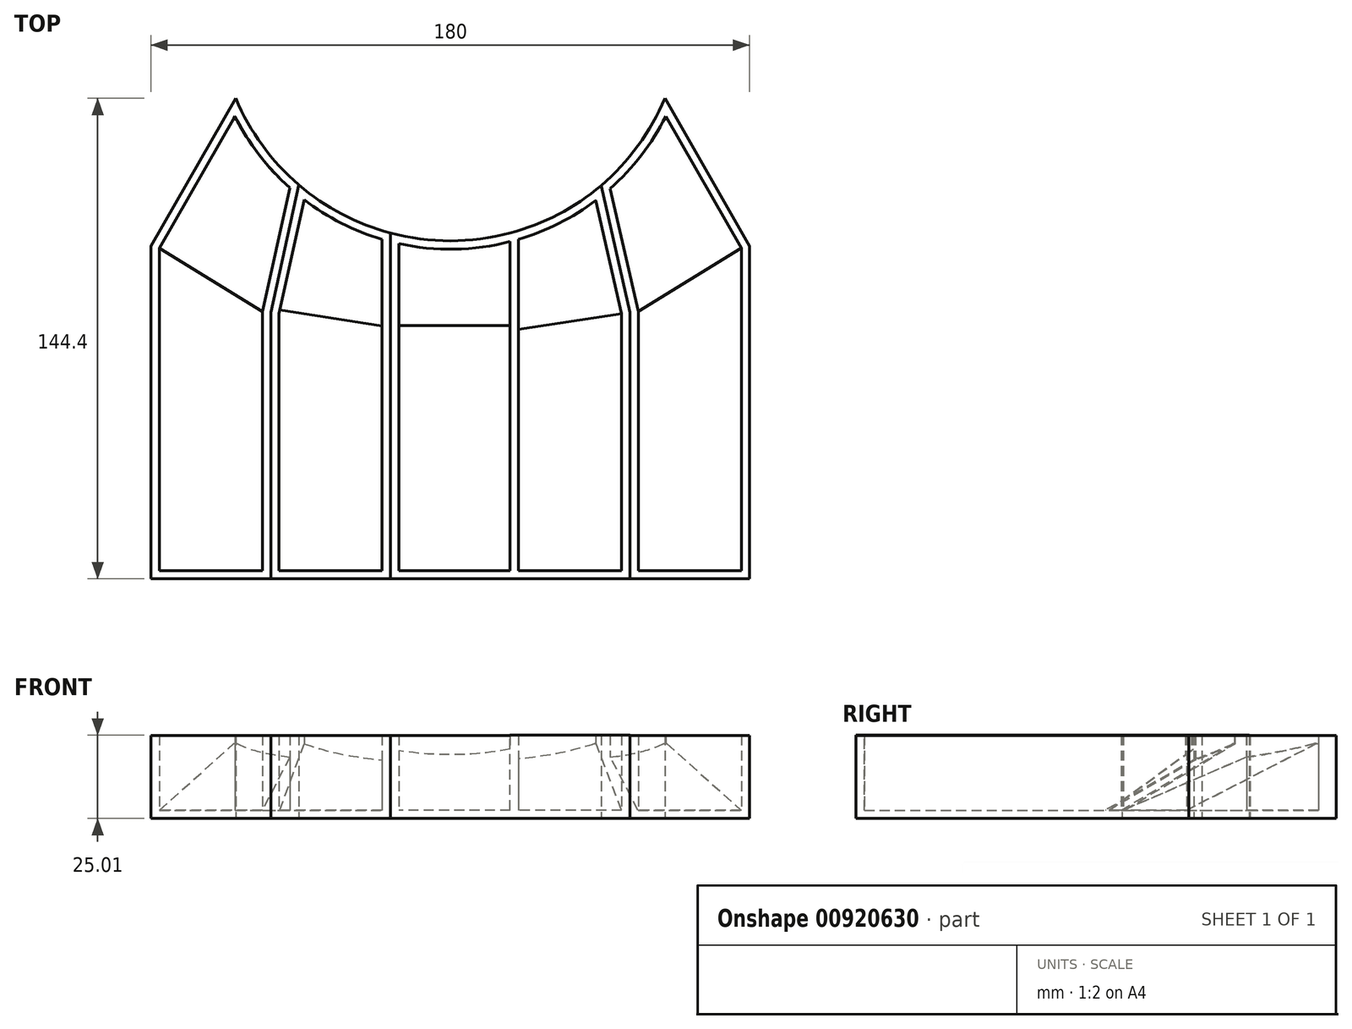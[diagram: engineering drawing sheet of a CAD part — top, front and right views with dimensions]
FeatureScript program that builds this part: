
annotation { "Feature Type Name" : "Feature", "Feature Type Description" : "" }
export const myFeature = defineFeature(function(context is Context, id is Id, definition is map)
    precondition{}
    {
        {
            var Q0;
            Q0=qCreatedBy(makeId("Top.planeOp"),FACE);
            var sketch = newSketch(context, id + "F0", { "sketchPlane" : qUnion([Q0])});
            skLineSegment(sketch, "E0", {"start": v(-90, -21.59) * mm, "end": v(90, -21.59) * mm});
            skLineSegment(sketch, "E1", {"start": v(-90, -21.59) * mm, "end": v(-90, 28.41) * mm});
            skLineSegment(sketch, "E2", {"start": v(90, 28.41) * mm, "end": v(90, -21.59) * mm});
            skLineSegment(sketch, "E3", {"start": v(-90, 28.41) * mm, "end": v(-90, 78.41) * mm});
            skLineSegment(sketch, "E4", {"start": v(-90, 78.41) * mm, "end": v(-64.5, 122.8) * mm});
            skLineSegment(sketch, "E5", {"start": v(90, 28.41) * mm, "end": v(90, 78.41) * mm});
            skLineSegment(sketch, "E6", {"start": v(90, 78.41) * mm, "end": v(64.5, 122.8) * mm});
            skLineSegment(sketch, "E7", {"start": v(-54, -21.59) * mm, "end": v(-54, 28.41) * mm});
            skLineSegment(sketch, "E8", {"start": v(-18, 28.41) * mm, "end": v(-18, -21.59) * mm});
            skLineSegment(sketch, "E9", {"start": v(54, 28.41) * mm, "end": v(54, -21.59) * mm});
            skLineSegment(sketch, "E10", {"start": v(18, 28.41) * mm, "end": v(18, -21.59) * mm});
            skArc(sketch, "E11", {"start": v(-64.5, 122.8) * mm, "mid": v(0, 79.98) * mm, "end": v(64.5, 122.8) * mm});
            skArc(sketch, "E12", {"start": v(-64.5, 122.8) * mm, "mid": v(0, 80.25) * mm, "end": v(64.5, 122.8) * mm});
            skLineSegment(sketch, "E13", {"start": v(-54, 28.41) * mm, "end": v(-54, 58.41) * mm});
            skLineSegment(sketch, "E14", {"start": v(-18, 28.41) * mm, "end": v(-18, 82.33) * mm});
            skLineSegment(sketch, "E15", {"start": v(18, 28.41) * mm, "end": v(18, 82.33) * mm});
            skLineSegment(sketch, "E16", {"start": v(54, 28.41) * mm, "end": v(54, 58.41) * mm});
            skLineSegment(sketch, "E17", {"start": v(-54, 58.41) * mm, "end": v(-45.52, 96.8) * mm});
            skLineSegment(sketch, "E18", {"start": v(45.27, 96.8) * mm, "end": v(54, 58.41) * mm});
            skLineSegment(sketch, "E19", {"start": v(-90, 28.41) * mm, "end": v(-54, 28.41) * mm});
            skLineSegment(sketch, "E20", {"start": v(-18, 28.41) * mm, "end": v(-54, 28.41) * mm});
            skLineSegment(sketch, "E21", {"start": v(-18, 28.41) * mm, "end": v(18, 28.41) * mm});
            skLineSegment(sketch, "E22", {"start": v(54, 28.41) * mm, "end": v(18, 28.41) * mm});
            skLineSegment(sketch, "E23", {"start": v(54, 28.41) * mm, "end": v(90, 28.41) * mm});
            skLineSegment(sketch, "E24", {"start": v(-54, 58.41) * mm, "end": v(-18, 55.37) * mm});
            skLineSegment(sketch, "E25", {"start": v(-18, 55.37) * mm, "end": v(18, 55.37) * mm});
            skLineSegment(sketch, "E26", {"start": v(18, 55.37) * mm, "end": v(54, 58.41) * mm});
            skSolve(sketch);
        }
        {
            var Q0;
            {var subQ3=sQuery(id+"F0.wireOp",EDGE,"E3");Q0=makeQuery(id+"F0.imprint","IMPRINT",FACE,{"disambiguationData":[TD([[makeQuery(id+"F0.imprint","IMPRINT",EDGE,{"derivedFrom":subQ3}),-1.0]])]});}
            var Q1;
            {var subQ0=sQuery(id+"F0.wireOp",EDGE,"E1");Q1=makeQuery(id+"F0.imprint","IMPRINT",FACE,{"disambiguationData":[TD([[makeQuery(id+"F0.imprint","IMPRINT",EDGE,{"derivedFrom":subQ0}),-1.0]])]});}
            var Q2;
            Q2=sQuery(id+"F0.wireOp",EDGE,"E4");
            var Q3;
            Q3=sQuery(id+"F0.wireOp",EDGE,"E3");
            var Q4;
            Q4=sQuery(id+"F0.wireOp",EDGE,"E11");
            var Q5;
            Q5=sQuery(id+"F0.wireOp",EDGE,"E17");
            var Q6;
            Q6=sQuery(id+"F0.wireOp",EDGE,"E18");
            var Q7;
            Q7=sQuery(id+"F0.wireOp",EDGE,"E6");
            var Q8;
            Q8=sQuery(id+"F0.wireOp",EDGE,"E5");
            var Q9;
            Q9=sQuery(id+"F0.wireOp",EDGE,"E15");
            var Q10;
            Q10=sQuery(id+"F0.wireOp",EDGE,"E14");
            var Q11;
            Q11=sQuery(id+"F0.wireOp",EDGE,"E13");
            var Q12;
            Q12=sQuery(id+"F0.wireOp",EDGE,"E16");
            var Q13;
            Q13=sQuery(id+"F0.wireOp",EDGE,"E2");
            var Q14;
            Q14=sQuery(id+"F0.wireOp",EDGE,"E0");
            var Q15;
            Q15=sQuery(id+"F0.wireOp",EDGE,"E9");
            var Q16;
            Q16=sQuery(id+"F0.wireOp",EDGE,"E10");
            var Q17;
            Q17=sQuery(id+"F0.wireOp",EDGE,"E8");
            var Q18;
            Q18=sQuery(id+"F0.wireOp",EDGE,"E7");
            extrude(context, id + "F1", {"entities" : qUnion([Q0, Q1]), "surfaceEntities" : qUnion([Q2, Q3, Q4, Q5, Q6, Q7, Q8, Q9, Q10, Q11, Q12, Q13, Q14, Q15, Q16, Q17, Q18]), "depth" : 25 * mm, "offsetDistance" : 25 * mm});
        }
        {
            var Q0;
            Q0=makeQuery(id+"F1.opExtrude","CAP_FACE",FACE,{"disambiguationData":[OSD([sQuery(id+"F0.wireOp",EDGE,"E0"),sQuery(id+"F0.wireOp",EDGE,"E1"),sQuery(id+"F0.wireOp",EDGE,"E2"),sQuery(id+"F0.wireOp",EDGE,"E3"),sQuery(id+"F0.wireOp",EDGE,"E4"),sQuery(id+"F0.wireOp",EDGE,"E5"),sQuery(id+"F0.wireOp",EDGE,"E6"),sQuery(id+"F0.wireOp",EDGE,"E11")])],"isStart":false});
            shell(context, id + "F2", {"entities" : qUnion([Q0]), "thickness" : 2.5 * mm});
        }
        {
            var Q0;
            {var subQ4=sQuery(id+"F0.wireOp",EDGE,"E5");Q0=makeQuery(id+"F0.imprint","IMPRINT",FACE,{"disambiguationData":[TD([[makeQuery(id+"F0.imprint","IMPRINT",EDGE,{"derivedFrom":subQ4}),1.0]])]});}
            var Q1;
            {var subQ0=sQuery(id+"F0.wireOp",EDGE,"E2");Q1=makeQuery(id+"F0.imprint","IMPRINT",FACE,{"disambiguationData":[TD([[makeQuery(id+"F0.imprint","IMPRINT",EDGE,{"derivedFrom":subQ0}),-1.0]])]});}
            extrude(context, id + "F3", {"entities" : qUnion([Q0, Q1]), "depth" : 25 * mm, "offsetDistance" : 25 * mm});
        }
        {
            var Q0;
            Q0=makeQuery(id+"F3.opExtrude","CAP_FACE",FACE,{"disambiguationData":[OSD([sQuery(id+"F0.wireOp",EDGE,"E0"),sQuery(id+"F0.wireOp",EDGE,"E2"),sQuery(id+"F0.wireOp",EDGE,"E5"),sQuery(id+"F0.wireOp",EDGE,"E6"),sQuery(id+"F0.wireOp",EDGE,"E9"),sQuery(id+"F0.wireOp",EDGE,"E11"),sQuery(id+"F0.wireOp",EDGE,"E16"),sQuery(id+"F0.wireOp",EDGE,"E18")])],"isStart":false});
            shell(context, id + "F4", {"entities" : qUnion([Q0]), "thickness" : 2.5 * mm});
        }
        {
            var Q0;
            {var subQ1=sQuery(id+"F0.wireOp",EDGE,"E15");Q0=makeQuery(id+"F0.imprint","IMPRINT",FACE,{"disambiguationData":[TD([[makeQuery(id+"F0.imprint","IMPRINT",EDGE,{"derivedFrom":subQ1}),-1.0]])]});}
            var Q1;
            {var subQ0=sQuery(id+"F0.wireOp",EDGE,"E9");Q1=makeQuery(id+"F0.imprint","IMPRINT",FACE,{"disambiguationData":[TD([[makeQuery(id+"F0.imprint","IMPRINT",EDGE,{"derivedFrom":subQ0}),-1.0]])]});}
            extrude(context, id + "F5", {"entities" : qUnion([Q0, Q1]), "depth" : 25 * mm, "offsetDistance" : 25 * mm});
        }
        {
            var Q0;
            Q0=makeQuery(id+"F5.opExtrude","CAP_FACE",FACE,{"disambiguationData":[OSD([sQuery(id+"F0.wireOp",EDGE,"E0"),sQuery(id+"F0.wireOp",EDGE,"E9"),sQuery(id+"F0.wireOp",EDGE,"E10"),sQuery(id+"F0.wireOp",EDGE,"E11"),sQuery(id+"F0.wireOp",EDGE,"E15"),sQuery(id+"F0.wireOp",EDGE,"E16"),sQuery(id+"F0.wireOp",EDGE,"E18")])],"isStart":false});
            shell(context, id + "F6", {"entities" : qUnion([Q0]), "thickness" : 2.5 * mm});
        }
        {
            var Q0;
            {var subQ0=sQuery(id+"F0.wireOp",EDGE,"E14");Q0=makeQuery(id+"F0.imprint","IMPRINT",FACE,{"disambiguationData":[TD([[makeQuery(id+"F0.imprint","IMPRINT",EDGE,{"derivedFrom":subQ0}),-1.0]])]});}
            var Q1;
            {var subQ0=sQuery(id+"F0.wireOp",EDGE,"E8");Q1=makeQuery(id+"F0.imprint","IMPRINT",FACE,{"disambiguationData":[TD([[makeQuery(id+"F0.imprint","IMPRINT",EDGE,{"derivedFrom":subQ0}),1.0]])]});}
            extrude(context, id + "F7", {"entities" : qUnion([Q0, Q1]), "operationType" : NewBodyOperationType.ADD, "depth" : 25 * mm, "offsetDistance" : 25 * mm});
        }
        {
            var Q0;
            Q0=makeQuery(id+"F7.opExtrude","CAP_FACE",FACE,{"disambiguationData":[OSD([sQuery(id+"F0.wireOp",EDGE,"E0"),sQuery(id+"F0.wireOp",EDGE,"E8"),sQuery(id+"F0.wireOp",EDGE,"E10"),sQuery(id+"F0.wireOp",EDGE,"E11"),sQuery(id+"F0.wireOp",EDGE,"E14"),sQuery(id+"F0.wireOp",EDGE,"E15")])],"isStart":false});
            shell(context, id + "F8", {"entities" : qUnion([Q0]), "thickness" : 2.5 * mm});
        }
        {
            var Q0;
            {var subQ3=sQuery(id+"F0.wireOp",EDGE,"E13");Q0=makeQuery(id+"F0.imprint","IMPRINT",FACE,{"disambiguationData":[TD([[makeQuery(id+"F0.imprint","IMPRINT",EDGE,{"derivedFrom":subQ3}),-1.0]])]});}
            var Q1;
            {var subQ0=sQuery(id+"F0.wireOp",EDGE,"E7");Q1=makeQuery(id+"F0.imprint","IMPRINT",FACE,{"disambiguationData":[TD([[makeQuery(id+"F0.imprint","IMPRINT",EDGE,{"derivedFrom":subQ0}),-1.0]])]});}
            var Q2;
            {var subQ3=sQuery(id+"F0.wireOp",EDGE,"E17");Q2=makeQuery(id+"F0.imprint","IMPRINT",FACE,{"disambiguationData":[TD([[makeQuery(id+"F0.imprint","IMPRINT",EDGE,{"derivedFrom":subQ3}),-1.0]])]});}
            extrude(context, id + "F9", {"entities" : qUnion([Q0, Q1, Q2]), "depth" : 25 * mm, "offsetDistance" : 25 * mm});
        }
        {
            var Q0;
            Q0=makeQuery(id+"F9.opExtrude","CAP_FACE",FACE,{"disambiguationData":[OSD([sQuery(id+"F0.wireOp",EDGE,"E0"),sQuery(id+"F0.wireOp",EDGE,"E7"),sQuery(id+"F0.wireOp",EDGE,"E8"),sQuery(id+"F0.wireOp",EDGE,"E11"),sQuery(id+"F0.wireOp",EDGE,"E13"),sQuery(id+"F0.wireOp",EDGE,"E14"),sQuery(id+"F0.wireOp",EDGE,"E17")])],"isStart":false});
            shell(context, id + "F10", {"entities" : qUnion([Q0]), "thickness" : 2.5 * mm});
        }
        {
            var Q0;
            Q0=makeQuery(id+"F2.opShell","OFFSET_FACE",FACE,{"disambiguationData":[OSD([sQuery(id+"F0.wireOp",EDGE,"E0"),sQuery(id+"F0.wireOp",EDGE,"E1"),sQuery(id+"F0.wireOp",EDGE,"E3"),sQuery(id+"F0.wireOp",EDGE,"E4"),sQuery(id+"F0.wireOp",EDGE,"E7"),sQuery(id+"F0.wireOp",EDGE,"E11"),sQuery(id+"F0.wireOp",EDGE,"E13"),sQuery(id+"F0.wireOp",EDGE,"E17")])]});
            var sketch = newSketch(context, id + "F11", { "sketchPlane" : qUnion([Q0])});
            skLineSegment(sketch, "E27", {"start": v(-87.5, 77.75) * mm, "end": v(-56.5, 58.69) * mm});
            skSolve(sketch);
        }
        {
            var Q0;
            Q0=makeQuery(id+"F4.opShell","OFFSET_FACE",FACE,{"disambiguationData":[OSD([sQuery(id+"F0.wireOp",EDGE,"E0"),sQuery(id+"F0.wireOp",EDGE,"E2"),sQuery(id+"F0.wireOp",EDGE,"E5"),sQuery(id+"F0.wireOp",EDGE,"E6"),sQuery(id+"F0.wireOp",EDGE,"E9"),sQuery(id+"F0.wireOp",EDGE,"E11"),sQuery(id+"F0.wireOp",EDGE,"E16"),sQuery(id+"F0.wireOp",EDGE,"E18")])]});
            var sketch = newSketch(context, id + "F12", { "sketchPlane" : qUnion([Q0])});
            skLineSegment(sketch, "E28", {"start": v(56.5, 58.7) * mm, "end": v(87.5, 77.75) * mm});
            skLineSegment(sketch, "E29", {"start": v(87.5, 77.75) * mm, "end": v(87.62, 77.1) * mm});
            skSolve(sketch);
        }
        {
            var Q0;
            Q0=makeQuery(id+"F11.imprint","IMPRINT",FACE,{"disambiguationData":[TD([[makeQuery(id+"F11.imprint","IMPRINT",EDGE,{"derivedFrom":sQuery(id+"F11.wireOp",EDGE,"E27")}),1.0]])]});
            extrude(context, id + "F13", {"entities" : qUnion([Q0]), "depth" : 20 * mm, "offsetDistance" : 25 * mm});
        }
        {
            var Q0;
            Q0=makeQuery(id+"F13.opExtrude","CAP_EDGE",EDGE,{"disambiguationData":[OSD([sQuery(id+"F11.wireOp",EDGE,"E27")])],"isStart":false});
            chamfer(context, id + "F14", {"entities" : qUnion([Q0]), "chamferType" : ChamferType.OFFSET_ANGLE, "width" : 45 * mm, "oppositeDirection" : false, "angle" : 24 * degree, "tangentPropagation" : true});
        }
        {
            var Q0;
            Q0=makeQuery(id+"F13.opExtrude","SWEPT_BODY",BODY,{"disambiguationData":[OSD([sQuery(id+"F0.wireOp",EDGE,"E4"),sQuery(id+"F0.wireOp",EDGE,"E11"),sQuery(id+"F0.wireOp",EDGE,"E17"),sQuery(id+"F11.wireOp",EDGE,"E27")])]});
            var Q1;
            Q1=makeQuery(id+"F8.opShell","OFFSET_FACE",FACE,{"disambiguationData":[OSD([sQuery(id+"F0.wireOp",EDGE,"E8"),sQuery(id+"F0.wireOp",EDGE,"E14")])]});
            mirror(context, id + "F15", {"entities" : qUnion([Q0]), "mirrorPlane" : qUnion([Q1])});
        }
        {
            var Q0;
            Q0=makeQuery(id+"F15.opPattern","COPY",BODY,{"derivedFrom":makeQuery(id+"F13.opExtrude","SWEPT_BODY",BODY,{"disambiguationData":[OSD([sQuery(id+"F0.wireOp",EDGE,"E4"),sQuery(id+"F0.wireOp",EDGE,"E11"),sQuery(id+"F0.wireOp",EDGE,"E17"),sQuery(id+"F11.wireOp",EDGE,"E27")])]}),"instanceName":"1"});
            deleteBodies(context, id + "F16", {"entities" : qUnion([Q0])});
        }
        {
            var Q0;
            Q0=makeQuery(id+"F8.opShell","OFFSET_FACE",FACE,{"disambiguationData":[OSD([sQuery(id+"F0.wireOp",EDGE,"E0"),sQuery(id+"F0.wireOp",EDGE,"E8"),sQuery(id+"F0.wireOp",EDGE,"E9"),sQuery(id+"F0.wireOp",EDGE,"E10"),sQuery(id+"F0.wireOp",EDGE,"E11"),sQuery(id+"F0.wireOp",EDGE,"E14"),sQuery(id+"F0.wireOp",EDGE,"E15"),sQuery(id+"F0.wireOp",EDGE,"E16"),sQuery(id+"F0.wireOp",EDGE,"E18")])]});
            var sketch = newSketch(context, id + "F17", { "sketchPlane" : qUnion([Q0])});
            skLineSegment(sketch, "E30", {"start": v(1.28, 77.49) * mm, "end": v(1.28, 72.56) * mm});
            skSolve(sketch);
        }
        {
            var Q0;
            Q0=makeQuery(id+"F12.imprint","IMPRINT",FACE,{"disambiguationData":[TD([[makeQuery(id+"F12.imprint","IMPRINT",EDGE,{"derivedFrom":sQuery(id+"F12.wireOp",EDGE,"E28")}),1.0]])]});
            extrude(context, id + "F18", {"entities" : qUnion([Q0]), "operationType" : NewBodyOperationType.ADD, "depth" : 20 * mm, "offsetDistance" : 25 * mm});
        }
        {
            var Q0;
            Q0=makeQuery(id+"F18.opExtrude","CAP_EDGE",EDGE,{"disambiguationData":[OSD([sQuery(id+"F12.wireOp",EDGE,"E28")])],"isStart":false});
            chamfer(context, id + "F19", {"entities" : qUnion([Q0]), "chamferType" : ChamferType.OFFSET_ANGLE, "width" : 45 * mm, "oppositeDirection" : false, "angle" : 24 * degree, "tangentPropagation" : true});
        }
        {
            var Q0;
            Q0=makeQuery(id+"F10.opShell","OFFSET_FACE",FACE,{"disambiguationData":[OSD([sQuery(id+"F0.wireOp",EDGE,"E0"),sQuery(id+"F0.wireOp",EDGE,"E7"),sQuery(id+"F0.wireOp",EDGE,"E8"),sQuery(id+"F0.wireOp",EDGE,"E11"),sQuery(id+"F0.wireOp",EDGE,"E13"),sQuery(id+"F0.wireOp",EDGE,"E14"),sQuery(id+"F0.wireOp",EDGE,"E17")])]});
            var sketch = newSketch(context, id + "F20", { "sketchPlane" : qUnion([Q0])});
            skLineSegment(sketch, "E31", {"start": v(-51.5, 58.14) * mm, "end": v(-20.5, 53.38) * mm});
            skSolve(sketch);
        }
        {
            var Q0;
            {var subQ0=sQuery(id+"F20.wireOp",EDGE,"E31");Q0=makeQuery(id+"F20.imprint","IMPRINT",FACE,{"disambiguationData":[TD([[makeQuery(id+"F20.imprint","IMPRINT",EDGE,{"derivedFrom":subQ0}),1.0]])]});}
            extrude(context, id + "F21", {"entities" : qUnion([Q0]), "operationType" : NewBodyOperationType.ADD, "depth" : 20 * mm, "offsetDistance" : 25 * mm});
        }
        {
            var Q0;
            Q0=makeQuery(id+"F21.opExtrude","CAP_EDGE",EDGE,{"disambiguationData":[OSD([sQuery(id+"F20.wireOp",EDGE,"E31")])],"isStart":false});
            chamfer(context, id + "F22", {"entities" : qUnion([Q0]), "chamferType" : ChamferType.OFFSET_ANGLE, "width" : 35 * mm, "oppositeDirection" : false, "angle" : 30.5 * degree, "tangentPropagation" : true});
        }
        {
            var Q0;
            Q0=makeQuery(id+"F6.opShell","OFFSET_FACE",FACE,{"disambiguationData":[OSD([sQuery(id+"F0.wireOp",EDGE,"E0"),sQuery(id+"F0.wireOp",EDGE,"E9"),sQuery(id+"F0.wireOp",EDGE,"E10"),sQuery(id+"F0.wireOp",EDGE,"E11"),sQuery(id+"F0.wireOp",EDGE,"E15"),sQuery(id+"F0.wireOp",EDGE,"E16"),sQuery(id+"F0.wireOp",EDGE,"E18")])]});
            var sketch = newSketch(context, id + "F23", { "sketchPlane" : qUnion([Q0])});
            skLineSegment(sketch, "E32", {"start": v(51.5, 58.13) * mm, "end": v(20.5, 53.37) * mm});
            skSolve(sketch);
        }
        {
            var Q0;
            {var subQ0=sQuery(id+"F23.wireOp",EDGE,"E32");Q0=makeQuery(id+"F23.imprint","IMPRINT",FACE,{"disambiguationData":[TD([[makeQuery(id+"F23.imprint","IMPRINT",EDGE,{"derivedFrom":subQ0}),-1.0]])]});}
            extrude(context, id + "F24", {"entities" : qUnion([Q0]), "operationType" : NewBodyOperationType.ADD, "depth" : 20 * mm, "offsetDistance" : 25 * mm});
        }
        {
            var Q0;
            Q0=makeQuery(id+"F24.opExtrude","CAP_EDGE",EDGE,{"disambiguationData":[OSD([sQuery(id+"F23.wireOp",EDGE,"E32")])],"isStart":false});
            chamfer(context, id + "F25", {"entities" : qUnion([Q0]), "chamferType" : ChamferType.OFFSET_ANGLE, "width" : 20 * mm, "oppositeDirection" : false, "angle" : 60 * degree, "tangentPropagation" : true});
        }
        {
            var Q0;
            {var subQ6=sQuery(id+"F0.wireOp",EDGE,"E0");Q0=makeQuery(id+"F17.imprint","IMPRINT",FACE,{"disambiguationData":[TD([[makeQuery(id+"F17.imprint","IMPRINT",EDGE,{"derivedFrom":makeQuery(id+"F8.opShell","OFFSET_EDGE",EDGE,{"disambiguationData":[OSD([subQ6]),TDD([makeQuery(id+"F7.boolean.opBoolean","MERGE",EDGE,{"derivedFrom":[makeQuery(id+"F5.opExtrude","CAP_EDGE",EDGE,{"disambiguationData":[OSD([subQ6])],"isStart":true}),makeQuery(id+"F7.opExtrude","CAP_EDGE",EDGE,{"disambiguationData":[OSD([subQ6])],"isStart":true})]})])]})}),1.0]])]});}
            var sketch = newSketch(context, id + "F26", { "sketchPlane" : qUnion([Q0])});
            skLineSegment(sketch, "E33", {"start": v(21.92, 54.54) * mm, "end": v(-15.99, 54.54) * mm});
            skSolve(sketch);
        }
        {
            var Q0;
            {var subQ0=sQuery(id+"F0.wireOp",EDGE,"E11");var subQ1=makeQuery(id+"F8.opShell","OFFSET_EDGE",EDGE,{"disambiguationData":[OSD([subQ0]),TDD([makeQuery(id+"F7.boolean.opBoolean","MERGE",EDGE,{"derivedFrom":[makeQuery(id+"F5.opExtrude","CAP_EDGE",EDGE,{"disambiguationData":[OSD([subQ0])],"isStart":true}),makeQuery(id+"F7.opExtrude","CAP_EDGE",EDGE,{"disambiguationData":[OSD([subQ0])],"isStart":true})]})])]});var subQ5=makeQuery(id+"F17.imprint","IMPRINT",VERTEX,{"derivedFrom":subQ1});var subQ6=makeQuery(id+"F17.imprint","IMPRINT",EDGE,{"disambiguationData":[TD([[subQ5,1.0]])],"derivedFrom":subQ1});Q0=makeQuery(id+"F26.imprint","IMPRINT",FACE,{"disambiguationData":[TD([[makeQuery(id+"F26.imprint","IMPRINT",EDGE,{"derivedFrom":subQ6}),-1.0]])]});}
            extrude(context, id + "F27", {"entities" : qUnion([Q0]), "operationType" : NewBodyOperationType.ADD, "depth" : 20 * mm, "offsetDistance" : 25 * mm});
        }
        {
            var Q0;
            Q0=makeQuery(id+"F27.opExtrude","CAP_EDGE",EDGE,{"disambiguationData":[OSD([sQuery(id+"F26.wireOp",EDGE,"E33")])],"isStart":false});
            chamfer(context, id + "F28", {"entities" : qUnion([Q0]), "chamferType" : ChamferType.OFFSET_ANGLE, "width" : 20 * mm, "oppositeDirection" : false, "angle" : 54 * degree, "tangentPropagation" : true});
        }
    });
